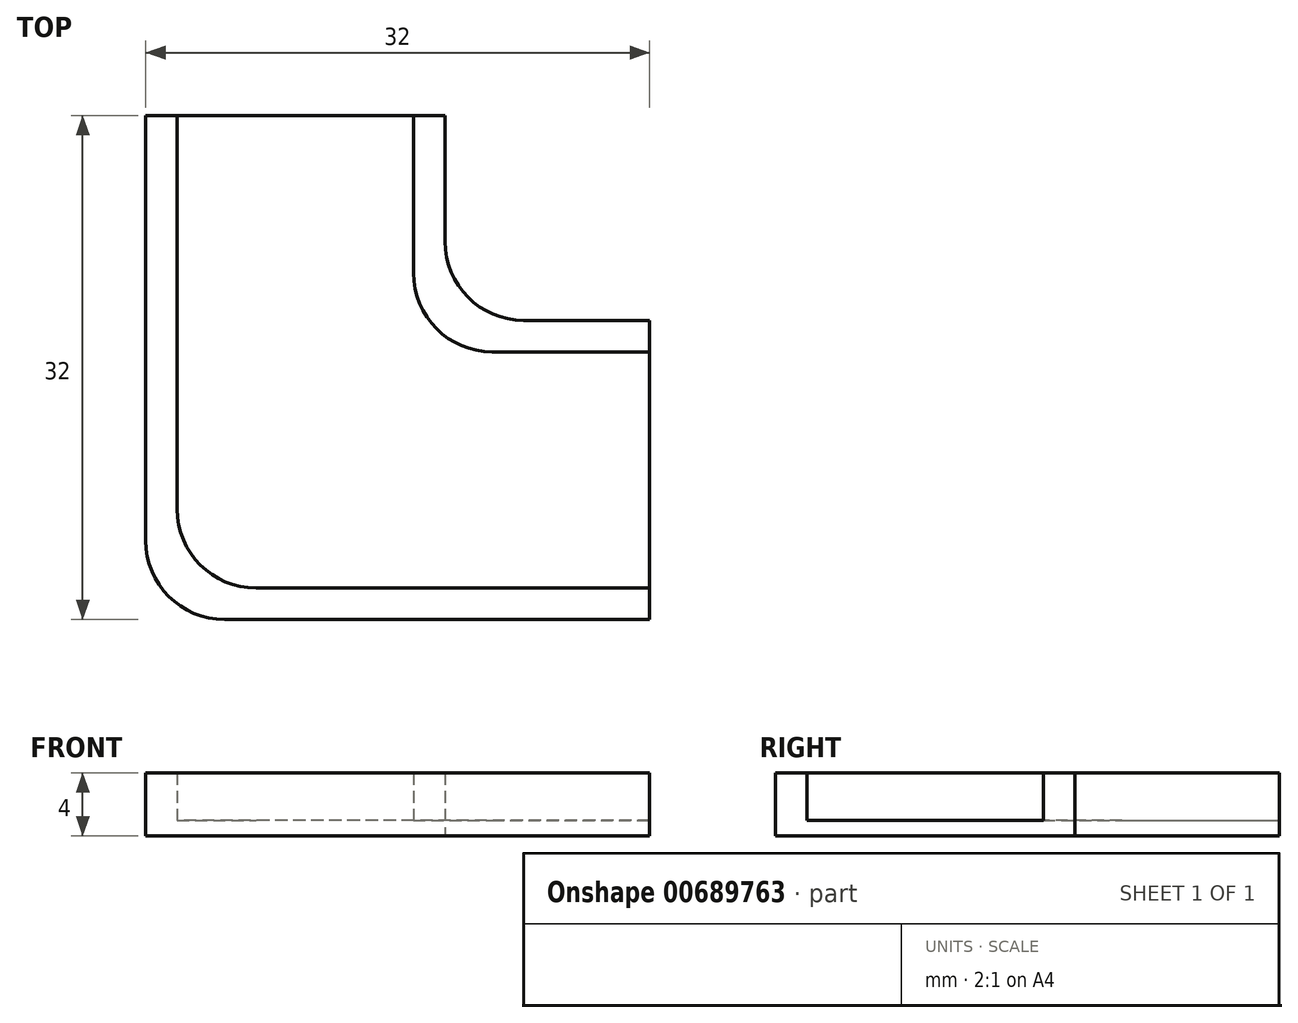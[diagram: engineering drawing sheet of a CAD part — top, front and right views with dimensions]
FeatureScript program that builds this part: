
annotation { "Feature Type Name" : "Feature", "Feature Type Description" : "" }
export const myFeature = defineFeature(function(context is Context, id is Id, definition is map)
    precondition{}
    {
        {
            var Q0;
            Q0=qCreatedBy(makeId("Top.planeOp"),FACE);
            var sketch = newSketch(context, id + "F0", { "sketchPlane" : qUnion([Q0])});
            skLineSegment(sketch, "E0.bottom", {"start": v(0, 0) * mm, "end": v(-15, 0) * mm});
            skLineSegment(sketch, "E0.top", {"start": v(0, 30) * mm, "end": v(-15, 30) * mm});
            skLineSegment(sketch, "E0.left", {"start": v(0, 15) * mm, "end": v(0, 30) * mm});
            skLineSegment(sketch, "E0.right", {"start": v(-15, 0) * mm, "end": v(-15, 30) * mm});
            skLineSegment(sketch, "E1.bottom", {"start": v(0, 0) * mm, "end": v(15, 0) * mm});
            skLineSegment(sketch, "E1.top", {"start": v(0, 15) * mm, "end": v(15, 15) * mm});
            skLineSegment(sketch, "E1.right", {"start": v(15, 0) * mm, "end": v(15, 15) * mm});
            skLineSegment(sketch, "E2.0", {"start": v(-17, -2) * mm, "end": v(-17, 30) * mm});
            skLineSegment(sketch, "E2.1", {"start": v(0, -2) * mm, "end": v(-17, -2) * mm});
            skLineSegment(sketch, "E2.2", {"start": v(0, -2) * mm, "end": v(15, -2) * mm});
            skLineSegment(sketch, "E3.0", {"start": v(2, 17) * mm, "end": v(15, 17) * mm});
            skLineSegment(sketch, "E3.1", {"start": v(2, 17) * mm, "end": v(2, 30) * mm});
            skLineSegment(sketch, "E4", {"start": v(-17, 30) * mm, "end": v(-15, 30) * mm});
            skLineSegment(sketch, "E5", {"start": v(2, 30) * mm, "end": v(0, 30) * mm});
            skLineSegment(sketch, "E6", {"start": v(15, 17) * mm, "end": v(15, 15) * mm});
            skLineSegment(sketch, "E7", {"start": v(15, 0) * mm, "end": v(15, -2) * mm});
            skSolve(sketch);
        }
        {
            var Q0;
            Q0=makeQuery(id+"F0.imprint","IMPRINT",FACE,{"disambiguationData":[TD([[makeQuery(id+"F0.imprint","IMPRINT",EDGE,{"derivedFrom":sQuery(id+"F0.wireOp",EDGE,"E0.bottom")}),-1.0]])]});
            extrude(context, id + "F1", {"entities" : qUnion([Q0]), "depth" : 1 * mm, "offsetDistance" : 25 * mm});
        }
        {
            var Q0;
            Q0=makeQuery(id+"F0.imprint","IMPRINT",FACE,{"disambiguationData":[TD([[makeQuery(id+"F0.imprint","IMPRINT",EDGE,{"derivedFrom":sQuery(id+"F0.wireOp",EDGE,"E0.bottom")}),1.0]])]});
            var Q1;
            Q1=makeQuery(id+"F0.imprint","IMPRINT",FACE,{"disambiguationData":[TD([[makeQuery(id+"F0.imprint","IMPRINT",EDGE,{"derivedFrom":sQuery(id+"F0.wireOp",EDGE,"E0.left")}),-1.0]])]});
            extrude(context, id + "F2", {"entities" : qUnion([Q0, Q1]), "operationType" : NewBodyOperationType.ADD, "depth" : 4 * mm, "offsetDistance" : 25 * mm});
        }
        {
            var Q0;
            Q0=makeQuery(id+"F2.opExtrude","SWEPT_EDGE",EDGE,{"disambiguationData":[OSD([sQuery(id+"F0.wireOp",EDGE,"E0.left"),sQuery(id+"F0.wireOp",EDGE,"E1.top")])]});
            var Q1;
            Q1=makeQuery(id+"F2.opExtrude","SWEPT_EDGE",EDGE,{"disambiguationData":[OSD([sQuery(id+"F0.wireOp",EDGE,"E2.0"),sQuery(id+"F0.wireOp",EDGE,"E2.1")])]});
            var Q2;
            Q2=makeQuery(id+"F2.opExtrude","SWEPT_EDGE",EDGE,{"disambiguationData":[OSD([sQuery(id+"F0.wireOp",EDGE,"E3.0"),sQuery(id+"F0.wireOp",EDGE,"E3.1")])]});
            var Q3;
            Q3=makeQuery(id+"F2.opExtrude","SWEPT_EDGE",EDGE,{"disambiguationData":[OSD([sQuery(id+"F0.wireOp",EDGE,"E0.bottom"),sQuery(id+"F0.wireOp",EDGE,"E0.right")])]});
            fillet(context, id + "F3", {"entities" : qUnion([Q0, Q1, Q2, Q3]), "radius" : 5 * mm, "tangentPropagation" : true, "allowEdgeOverflow" : false});
        }
    });
